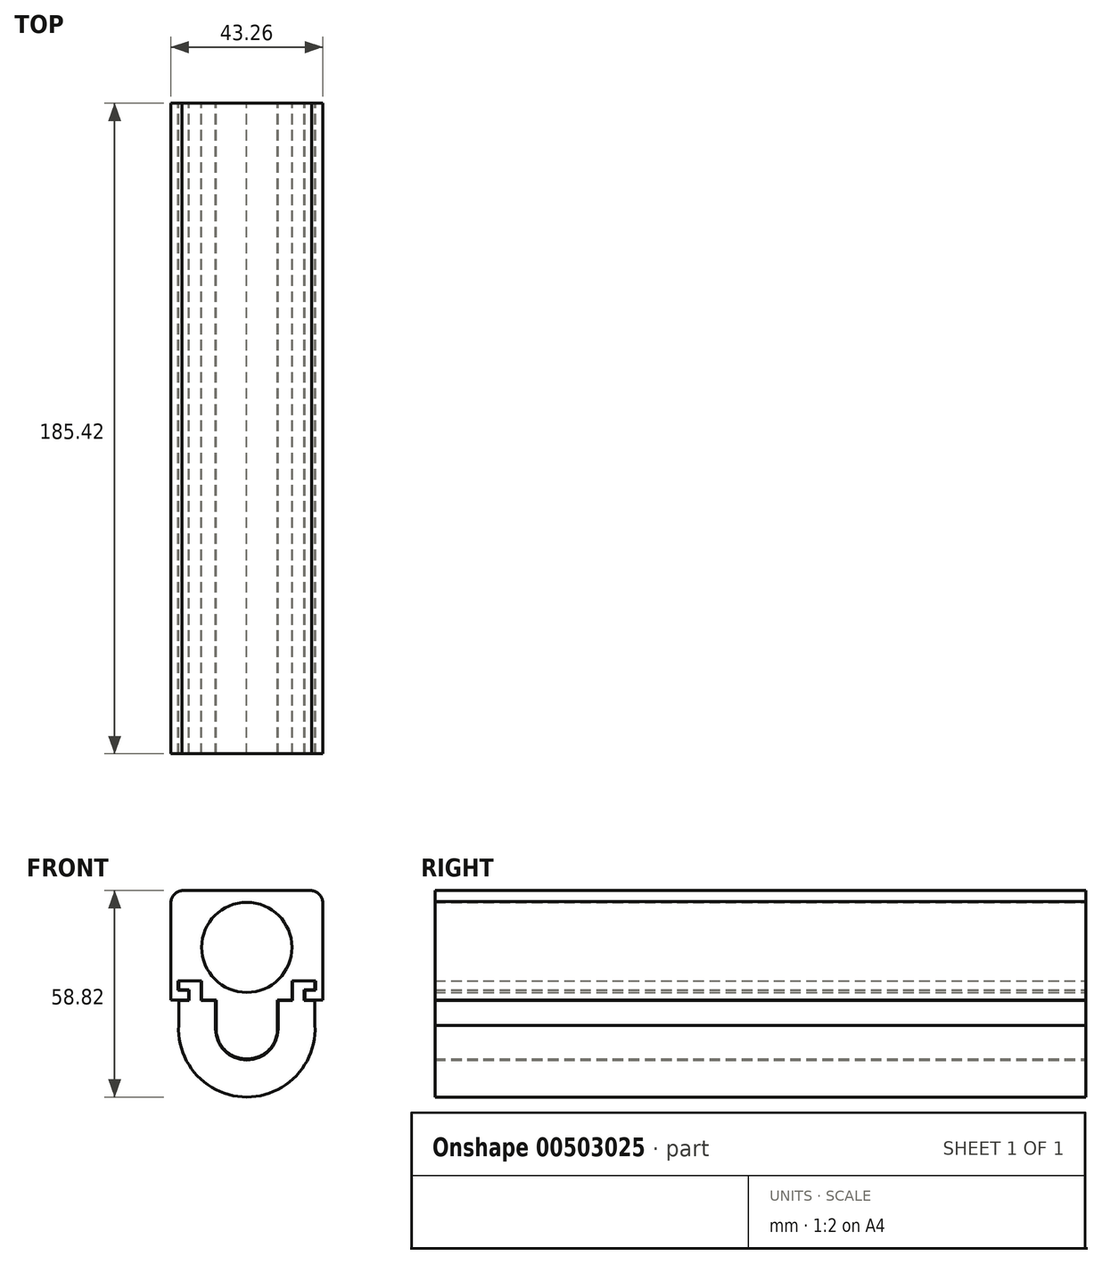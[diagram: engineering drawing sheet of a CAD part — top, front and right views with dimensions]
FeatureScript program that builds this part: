
annotation { "Feature Type Name" : "Feature", "Feature Type Description" : "" }
export const myFeature = defineFeature(function(context is Context, id is Id, definition is map)
    precondition{}
    {
        {
            var Q0;
            Q0=qCreatedBy(makeId("Front.planeOp"),FACE);
            var sketch = newSketch(context, id + "F0", { "sketchPlane" : qUnion([Q0])});
            skArc(sketch, "E0", {"start": v(-8.9, 0) * mm, "mid": v(0, -8.9) * mm, "end": v(8.9, 0) * mm});
            skCircle(sketch, "E1", {"center": v(0, 23.2) * mm, "radius": 12.85 * mm});
            skLineSegment(sketch, "E2", {"start": v(-8.9, 0) * mm, "end": v(-8.9, 8.06) * mm});
            skLineSegment(sketch, "E3", {"start": v(-8.9, 8.06) * mm, "end": v(-12.98, 8.06) * mm});
            skLineSegment(sketch, "E4", {"start": v(-12.98, 8.06) * mm, "end": v(-12.98, 13.6) * mm});
            skLineSegment(sketch, "E5", {"start": v(-12.98, 13.6) * mm, "end": v(-19.41, 13.6) * mm});
            skLineSegment(sketch, "E6", {"start": v(-19.41, 13.6) * mm, "end": v(-19.41, 11.17) * mm});
            skLineSegment(sketch, "E7", {"start": v(-19.41, 11.17) * mm, "end": v(-16.38, 11.17) * mm});
            skLineSegment(sketch, "E8", {"start": v(-16.38, 11.17) * mm, "end": v(-16.38, 8.06) * mm});
            skLineSegment(sketch, "E9", {"start": v(-16.38, 8.06) * mm, "end": v(-19.41, 8.06) * mm});
            skLineSegment(sketch, "E10", {"start": v(-19.41, 8.06) * mm, "end": v(-19.41, 0) * mm});
            skArc(sketch, "E11", {"start": v(-19.41, 0.97) * mm, "mid": v(0, -19.44) * mm, "end": v(19.41, 0.97) * mm});
            skLineSegment(sketch, "E12.MirrorCS", {"start": v(16.38, 11.17) * mm, "end": v(16.38, 8.06) * mm});
            skLineSegment(sketch, "E13.MirrorCS", {"start": v(19.41, 8.06) * mm, "end": v(19.41, 0) * mm});
            skLineSegment(sketch, "E14.MirrorCS", {"start": v(16.38, 8.06) * mm, "end": v(19.41, 8.06) * mm});
            skLineSegment(sketch, "E15.MirrorCS", {"start": v(19.41, 11.17) * mm, "end": v(16.38, 11.17) * mm});
            skLineSegment(sketch, "E16.MirrorCS", {"start": v(8.9, 0) * mm, "end": v(8.9, 8.06) * mm});
            skLineSegment(sketch, "E17.MirrorCS", {"start": v(12.98, 13.6) * mm, "end": v(19.41, 13.6) * mm});
            skLineSegment(sketch, "E18.MirrorCS", {"start": v(8.9, 8.06) * mm, "end": v(12.98, 8.06) * mm});
            skLineSegment(sketch, "E19.MirrorCS", {"start": v(19.41, 13.6) * mm, "end": v(19.41, 11.17) * mm});
            skLineSegment(sketch, "E20.MirrorCS", {"start": v(12.98, 8.06) * mm, "end": v(12.98, 13.6) * mm});
            skPoint(sketch, "E21.end.orphan", {"position": v(8.1, 0) * mm});
            skPoint(sketch, "E21.start.orphan", {"position": v(-8.1, 0) * mm});
            skLineSegment(sketch, "E22", {"start": v(-19.57, 11.04) * mm, "end": v(-16.54, 11.04) * mm});
            skLineSegment(sketch, "E23", {"start": v(-16.54, 11.04) * mm, "end": v(-16.54, 8.21) * mm});
            skLineSegment(sketch, "E24", {"start": v(-16.54, 8.21) * mm, "end": v(-21.63, 8.21) * mm});
            skPoint(sketch, "E25.orphan", {"position": v(-19.41, 39.49) * mm});
            skPoint(sketch, "E26.end.orphan", {"position": v(0, 39.49) * mm});
            skLineSegment(sketch, "E27", {"start": v(-21.63, 8.21) * mm, "end": v(-21.63, 36.29) * mm});
            skLineSegment(sketch, "E28", {"start": v(-18.42, 39.38) * mm, "end": v(0, 39.38) * mm});
            skArc(sketch, "E29", {"start": v(-18.42, 39.38) * mm, "mid": v(-20.57, 38.4) * mm, "end": v(-21.63, 36.29) * mm});
            skLineSegment(sketch, "E30", {"start": v(-19.57, 11.04) * mm, "end": v(-19.57, 13.72) * mm});
            skLineSegment(sketch, "E31", {"start": v(-19.57, 13.72) * mm, "end": v(-12.91, 13.72) * mm});
            skLineSegment(sketch, "E32", {"start": v(-12.91, 13.72) * mm, "end": v(-12.91, 8.17) * mm});
            skLineSegment(sketch, "E33", {"start": v(-12.91, 8.17) * mm, "end": v(-8.74, 8.17) * mm});
            skLineSegment(sketch, "E34", {"start": v(-8.74, 8.17) * mm, "end": v(-8.74, 0) * mm});
            skArc(sketch, "E35", {"start": v(-8.74, 0) * mm, "mid": v(-6.17, -6.11) * mm, "end": v(0, -8.55) * mm});
            skLineSegment(sketch, "E36.MirrorCS", {"start": v(16.54, 11.04) * mm, "end": v(16.54, 8.21) * mm});
            skLineSegment(sketch, "E37.MirrorCS", {"start": v(12.91, 8.17) * mm, "end": v(8.74, 8.17) * mm});
            skLineSegment(sketch, "E38.MirrorCS", {"start": v(19.57, 11.04) * mm, "end": v(16.54, 11.04) * mm});
            skLineSegment(sketch, "E39.MirrorCS", {"start": v(12.91, 13.72) * mm, "end": v(12.91, 8.17) * mm});
            skLineSegment(sketch, "E40.MirrorCS", {"start": v(19.57, 11.04) * mm, "end": v(19.57, 13.72) * mm});
            skArc(sketch, "E41.MirrorCS", {"start": v(18.42, 39.38) * mm, "mid": v(20.57, 38.4) * mm, "end": v(21.63, 36.29) * mm});
            skLineSegment(sketch, "E42.MirrorCS", {"start": v(16.54, 8.21) * mm, "end": v(21.63, 8.21) * mm});
            skLineSegment(sketch, "E43.MirrorCS", {"start": v(19.57, 13.72) * mm, "end": v(12.91, 13.72) * mm});
            skLineSegment(sketch, "E44.MirrorCS", {"start": v(21.63, 8.21) * mm, "end": v(21.63, 36.29) * mm});
            skLineSegment(sketch, "E45.MirrorCS", {"start": v(18.42, 39.38) * mm, "end": v(0, 39.38) * mm});
            skLineSegment(sketch, "E46.MirrorCS", {"start": v(8.74, 8.17) * mm, "end": v(8.74, 0) * mm});
            skPoint(sketch, "E47.MirrorP", {"position": v(19.41, 39.49) * mm});
            skArc(sketch, "E48.MirrorCS", {"start": v(8.74, 0) * mm, "mid": v(6.17, -6.11) * mm, "end": v(0, -8.55) * mm});
            skSolve(sketch);
        }
        {
            var Q0;
            Q0 = qSketchRegion(id + "F0", true);
            extrude(context, id + "F1", {"entities" : qUnion([Q0]), "depth" : 185.42 * mm});
        }
    });
